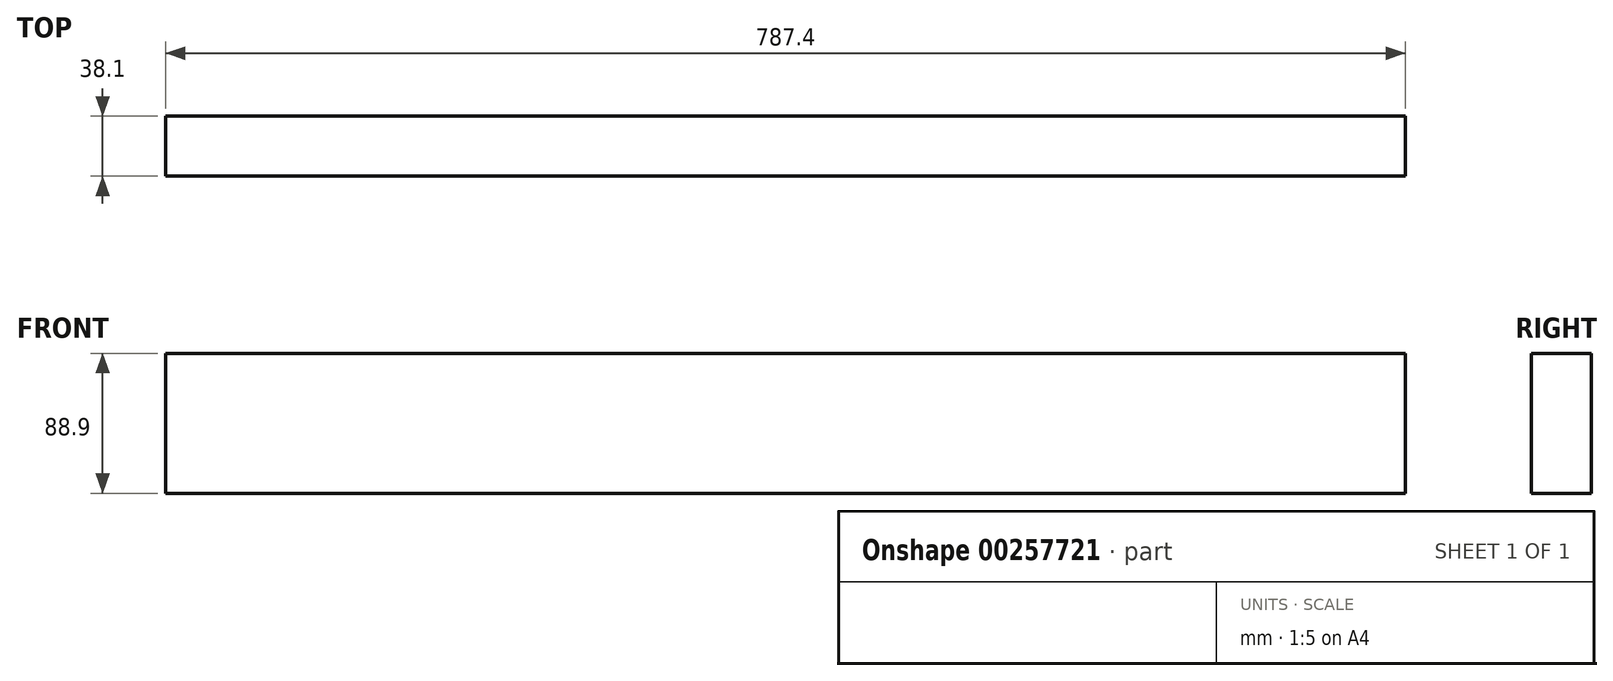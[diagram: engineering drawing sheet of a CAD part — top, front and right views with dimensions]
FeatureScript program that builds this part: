
annotation { "Feature Type Name" : "Feature", "Feature Type Description" : "" }
export const myFeature = defineFeature(function(context is Context, id is Id, definition is map)
    precondition{}
    {
        {
            var Q0;
            Q0=qCreatedBy(makeId("Top.planeOp"),FACE);
            var sketch = newSketch(context, id + "F0", { "sketchPlane" : qUnion([Q0])});
            skLineSegment(sketch, "E0.bottom", {"start": v(-393.7, 19.05) * mm, "end": v(393.7, 19.05) * mm});
            skLineSegment(sketch, "E0.top", {"start": v(-393.7, -19.05) * mm, "end": v(393.7, -19.05) * mm});
            skLineSegment(sketch, "E0.left", {"start": v(-393.7, 19.05) * mm, "end": v(-393.7, -19.05) * mm});
            skLineSegment(sketch, "E0.right", {"start": v(393.7, 19.05) * mm, "end": v(393.7, -19.05) * mm});
            skSolve(sketch);
        }
        {
            var Q0;
            Q0=makeQuery(id+"F0.imprint","IMPRINT",FACE,{"disambiguationData":[TD([[makeQuery(id+"F0.imprint","IMPRINT",EDGE,{"derivedFrom":sQuery(id+"F0.wireOp",EDGE,"E0.bottom")}),-1.0]])]});
            extrude(context, id + "F1", {"entities" : qUnion([Q0]), "endBound" : BoundingType.SYMMETRIC, "depth" : 88.9 * mm});
        }
    });
